# Revit family: Servo_Easy_Arm_Gorbel_EA-F
name_source: partatom
category: Specialty Equipment
units: mm (PartAtom-declared; Revit-internal decimal feet)

## family parameters
Always vertical = No
Cut with Voids When Loaded = No
Enable Cutting in Views = No
Maintain Annotation Orientation = No
OmniClass Number = 23.50.30.37.11
OmniClass Title = Cranes
Part Type = Normal
Room Calculation Point = No
Round Connector Dimension = Use Diameter
Shared = No
Work Plane-Based = Yes

## types (1)
- Servo_Easy_Arm_Gorbel_EA-F
    Assembly Code = D1090300
    Capacity (Lbs) = 0.00 kip
    Default Elevation = 4' - 0"
    Description = Gorbel
    Expected Lifespan (Years) = 0
    Fixture Material = Steel
    HUH = 6' - 0"
    Installation-Fabrication = https://www.gorbel.com
    Keynote = 14600
    Maintenance Schedule (Months) = 0
    Manufacturer = Gorbel Inc
    Manufacturer Fax = 800-828-1808;585-924-6273
    Manufacturer Website = https://www.gorbel.com
    Model = As Specified
    Post Height = 8' - 10 3/8"
    Prim Angle = 90.00°
    Product Data = http://arcat.com
    Product Properties = https://www.gorbel.com
    Revision = R1_05-2011
    Sales Information = https://www.gorbel.com
    Sec Angle = 180.00°
    Send Message = http://www.arcat.com
    Span = 6' - 0"
    Specification = http://www.arcat.com
    Test Data = https://www.gorbel.com
    URL = https://www.gorbel.com
    Warranty Duration (Years) = 0

## geometry (parser evidence)
native form markers: Sweep x4
no freeform markers — native parametric forms only
